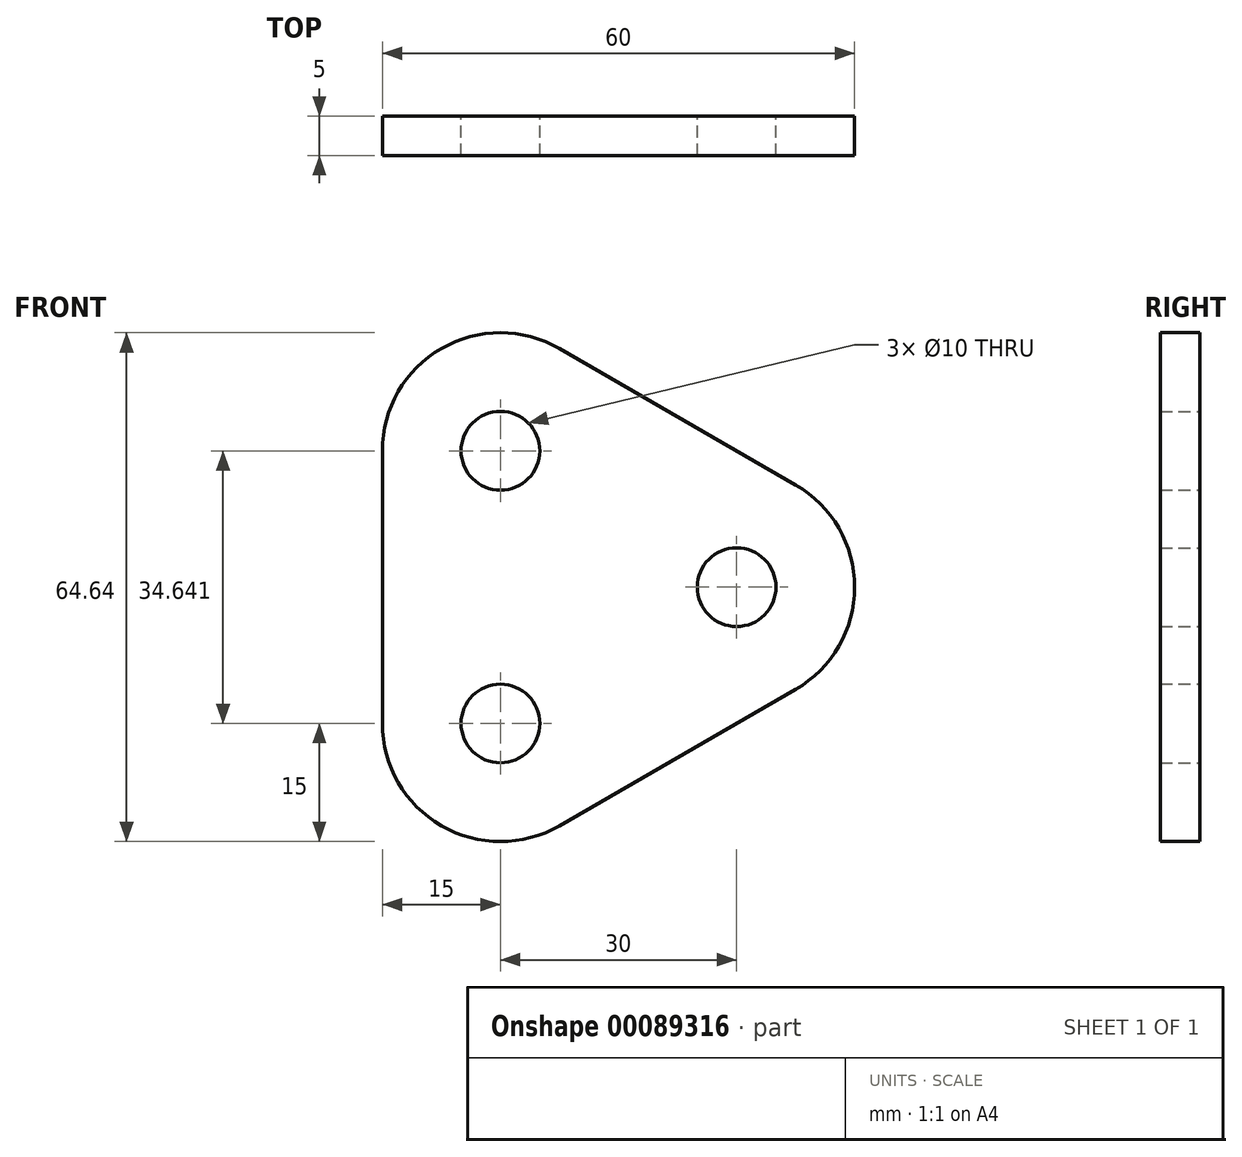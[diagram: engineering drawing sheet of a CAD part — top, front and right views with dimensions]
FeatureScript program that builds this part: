
annotation { "Feature Type Name" : "Feature", "Feature Type Description" : "" }
export const myFeature = defineFeature(function(context is Context, id is Id, definition is map)
    precondition{}
    {
        {
            var Q0;
            Q0=qCreatedBy(makeId("Front.planeOp"),FACE);
            var sketch = newSketch(context, id + "F0", { "sketchPlane" : qUnion([Q0])});
            skCircle(sketch, "E0", {"center": v(0, 0) * mm, "radius": 20 * mm, "construction": true});
            skCircle(sketch, "E1", {"center": v(20, 0) * mm, "radius": 5 * mm});
            skCircle(sketch, "E2.1.0", {"center": v(-10, -17.32) * mm, "radius": 5 * mm});
            skCircle(sketch, "E2.2.0", {"center": v(-10, 17.32) * mm, "radius": 5 * mm});
            skLineSegment(sketch, "E2.anchor1", {"start": v(0, 0) * mm, "end": v(20, 0) * mm, "construction": true});
            skLineSegment(sketch, "E2.anchor2", {"start": v(0, 0) * mm, "end": v(-10, 17.32) * mm, "construction": true});
            skArc(sketch, "E3", {"start": v(-25, 17.32) * mm, "mid": v(-17.5, 30.31) * mm, "end": v(-2.5, 30.31) * mm});
            skArc(sketch, "E4", {"start": v(27.5, 13) * mm, "mid": v(35, 0) * mm, "end": v(27.5, -13) * mm});
            skArc(sketch, "E5", {"start": v(-2.5, -30.31) * mm, "mid": v(-17.5, -30.31) * mm, "end": v(-25, -17.32) * mm});
            skLineSegment(sketch, "E6", {"start": v(-25, 17.32) * mm, "end": v(-25, -17.32) * mm});
            skLineSegment(sketch, "E7", {"start": v(-2.5, -30.31) * mm, "end": v(27.5, -13) * mm});
            skLineSegment(sketch, "E8", {"start": v(27.5, 13) * mm, "end": v(-2.5, 30.31) * mm});
            skSolve(sketch);
        }
        {
            var Q0;
            Q0 = qSketchRegion(id + "F0", true);
            extrude(context, id + "F1", {"entities" : qUnion([Q0]), "depth" : 5 * mm});
        }
    });
